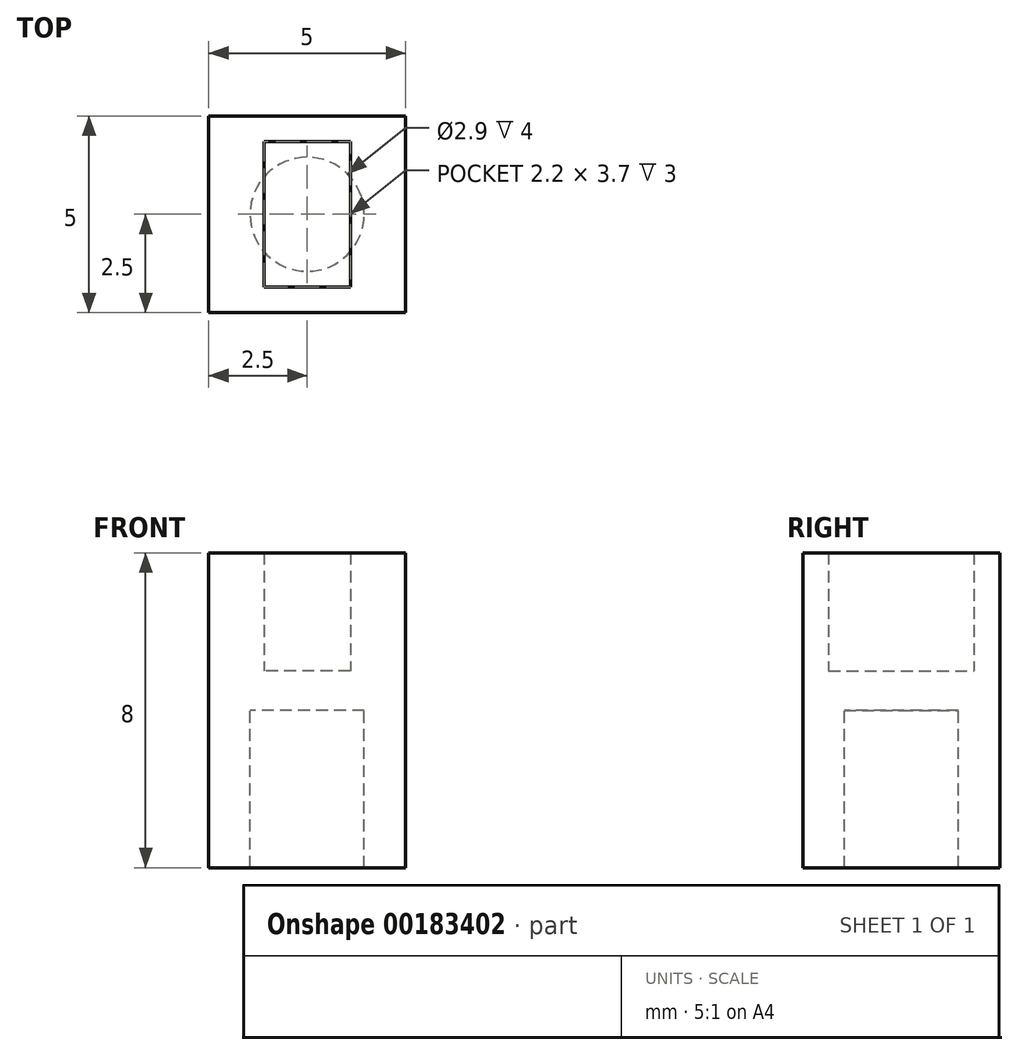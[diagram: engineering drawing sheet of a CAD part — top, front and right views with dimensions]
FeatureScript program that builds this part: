
annotation { "Feature Type Name" : "Feature", "Feature Type Description" : "" }
export const myFeature = defineFeature(function(context is Context, id is Id, definition is map)
    precondition{}
    {
        {
            var Q0;
            Q0=qCreatedBy(makeId("Top.planeOp"),FACE);
            var sketch = newSketch(context, id + "F0", { "sketchPlane" : qUnion([Q0])});
            skLineSegment(sketch, "E0.bottom", {"start": v(2.5, 2.5) * mm, "end": v(-2.5, 2.5) * mm});
            skLineSegment(sketch, "E0.top", {"start": v(2.5, -2.5) * mm, "end": v(-2.5, -2.5) * mm});
            skLineSegment(sketch, "E0.left", {"start": v(2.5, 2.5) * mm, "end": v(2.5, -2.5) * mm});
            skLineSegment(sketch, "E0.right", {"start": v(-2.5, 2.5) * mm, "end": v(-2.5, -2.5) * mm});
            skPoint(sketch, "E0.middle", {"position": v(0, 0) * mm});
            skSolve(sketch);
        }
        {
            var Q0;
            Q0=makeQuery(id+"F0.imprint","IMPRINT",FACE,{"disambiguationData":[TD([[makeQuery(id+"F0.imprint","IMPRINT",EDGE,{"derivedFrom":sQuery(id+"F0.wireOp",EDGE,"E0.bottom")}),1.0]])]});
            extrude(context, id + "F1", {"entities" : qUnion([Q0]), "depth" : 5 * mm});
        }
        {
            var Q0;
            Q0=makeQuery(id+"F1.opExtrude","CAP_FACE",FACE,{"disambiguationData":[OSD([sQuery(id+"F0.wireOp",EDGE,"E0.bottom"),sQuery(id+"F0.wireOp",EDGE,"E0.top"),sQuery(id+"F0.wireOp",EDGE,"E0.left"),sQuery(id+"F0.wireOp",EDGE,"E0.right")])],"isStart":false});
            var sketch = newSketch(context, id + "F2", { "sketchPlane" : qUnion([Q0])});
            skCircle(sketch, "E1", {"center": v(0, 0) * mm, "radius": 1.45 * mm});
            skSolve(sketch);
        }
        {
            var Q0;
            Q0=makeQuery(id+"F2.imprint","IMPRINT",FACE,{"disambiguationData":[TD([[makeQuery(id+"F2.imprint","IMPRINT",EDGE,{"derivedFrom":sQuery(id+"F2.wireOp",EDGE,"E1")}),1.0]])]});
            var Q1;
            Q1=sQuery(id+"F2.wireOp",EDGE,"E1");
            extrude(context, id + "F3", {"entities" : qUnion([Q0]), "operationType" : NewBodyOperationType.REMOVE, "surfaceEntities" : qUnion([Q1]), "endBound" : BoundingType.THROUGH_ALL, "oppositeDirection" : true, "depth" : 25 * mm});
        }
        {
            var Q0;
            Q0=makeQuery(id+"F1.opExtrude","CAP_FACE",FACE,{"disambiguationData":[OSD([sQuery(id+"F0.wireOp",EDGE,"E0.bottom"),sQuery(id+"F0.wireOp",EDGE,"E0.top"),sQuery(id+"F0.wireOp",EDGE,"E0.left"),sQuery(id+"F0.wireOp",EDGE,"E0.right")])],"isStart":false});
            var sketch = newSketch(context, id + "F4", { "sketchPlane" : qUnion([Q0])});
            skLineSegment(sketch, "E2.bottom", {"start": v(2.5, -2.5) * mm, "end": v(-2.5, -2.5) * mm});
            skLineSegment(sketch, "E2.top", {"start": v(2.5, 2.5) * mm, "end": v(-2.5, 2.5) * mm});
            skLineSegment(sketch, "E2.left", {"start": v(2.5, -2.5) * mm, "end": v(2.5, 2.5) * mm});
            skLineSegment(sketch, "E2.right", {"start": v(-2.5, -2.5) * mm, "end": v(-2.5, 2.5) * mm});
            skPoint(sketch, "E2.middle", {"position": v(0, 0) * mm});
            skLineSegment(sketch, "E3.bottom", {"start": v(1.1, -1.85) * mm, "end": v(-1.1, -1.85) * mm});
            skLineSegment(sketch, "E3.top", {"start": v(1.1, 1.85) * mm, "end": v(-1.1, 1.85) * mm});
            skLineSegment(sketch, "E3.left", {"start": v(1.1, -1.85) * mm, "end": v(1.1, 1.85) * mm});
            skLineSegment(sketch, "E3.right", {"start": v(-1.1, -1.85) * mm, "end": v(-1.1, 1.85) * mm});
            skSolve(sketch);
        }
        {
            var Q0;
            Q0 = qSketchRegion(id + "F4", true);
            extrude(context, id + "F5", {"entities" : qUnion([Q0]), "operationType" : NewBodyOperationType.ADD, "depth" : 3 * mm});
        }
        {
            var Q0;
            Q0=makeQuery(id+"F4.imprint","IMPRINT",FACE,{"disambiguationData":[TD([[makeQuery(id+"F4.imprint","IMPRINT",EDGE,{"derivedFrom":sQuery(id+"F4.wireOp",EDGE,"E2.bottom")}),-1.0]])]});
            var Q1;
            {var subQ0=sQuery(id+"F4.wireOp",EDGE,"E3.top");Q1=makeQuery(id+"F4.imprint","IMPRINT",FACE,{"disambiguationData":[TD([[makeQuery(id+"F4.imprint","IMPRINT",EDGE,{"derivedFrom":subQ0}),1.0]])]});}
            var Q2;
            {var subQ0=sQuery(id+"F4.wireOp",EDGE,"E3.right");var subQ1=makeQuery(id+"F3.boolean.opBoolean","COPY",EDGE,{"derivedFrom":makeQuery(id+"F3.opExtrude","CAP_EDGE",EDGE,{"disambiguationData":[OSD([sQuery(id+"F2.wireOp",EDGE,"E1")])],"isStart":true})});var subQ2=makeQuery(id+"F4.imprint","INTERSECT",VERTEX,{"disambiguationData":[OD(0.0)],"derivedFrom":[subQ1,subQ0]});Q2=makeQuery(id+"F4.imprint","IMPRINT",FACE,{"disambiguationData":[TD([[makeQuery(id+"F4.imprint","IMPRINT",EDGE,{"disambiguationData":[TD([[subQ2,-1.0]])],"derivedFrom":subQ0}),1.0]])]});}
            var Q3;
            {var subQ0=sQuery(id+"F4.wireOp",EDGE,"E3.left");var subQ1=makeQuery(id+"F3.boolean.opBoolean","COPY",EDGE,{"derivedFrom":makeQuery(id+"F3.opExtrude","CAP_EDGE",EDGE,{"disambiguationData":[OSD([sQuery(id+"F2.wireOp",EDGE,"E1")])],"isStart":true})});var subQ2=makeQuery(id+"F4.imprint","INTERSECT",VERTEX,{"disambiguationData":[OD(0.0)],"derivedFrom":[subQ1,subQ0]});Q3=makeQuery(id+"F4.imprint","IMPRINT",FACE,{"disambiguationData":[TD([[makeQuery(id+"F4.imprint","IMPRINT",EDGE,{"disambiguationData":[TD([[subQ2,-1.0]])],"derivedFrom":subQ0}),1.0]])]});}
            var Q4;
            {var subQ0=sQuery(id+"F4.wireOp",EDGE,"E3.left");var subQ1=makeQuery(id+"F3.boolean.opBoolean","COPY",EDGE,{"derivedFrom":makeQuery(id+"F3.opExtrude","CAP_EDGE",EDGE,{"disambiguationData":[OSD([sQuery(id+"F2.wireOp",EDGE,"E1")])],"isStart":true})});var subQ2=makeQuery(id+"F4.imprint","INTERSECT",VERTEX,{"disambiguationData":[OD(0.0)],"derivedFrom":[subQ1,subQ0]});Q4=makeQuery(id+"F4.imprint","IMPRINT",FACE,{"disambiguationData":[TD([[makeQuery(id+"F4.imprint","IMPRINT",EDGE,{"disambiguationData":[TD([[subQ2,-1.0]])],"derivedFrom":subQ0}),-1.0]])]});}
            var Q5;
            {var subQ0=sQuery(id+"F4.wireOp",EDGE,"E3.bottom");Q5=makeQuery(id+"F4.imprint","IMPRINT",FACE,{"disambiguationData":[TD([[makeQuery(id+"F4.imprint","IMPRINT",EDGE,{"derivedFrom":subQ0}),-1.0]])]});}
            extrude(context, id + "F6", {"entities" : qUnion([Q0, Q1, Q2, Q3, Q4, Q5]), "operationType" : NewBodyOperationType.ADD, "oppositeDirection" : true, "depth" : 1 * mm});
        }
    });
